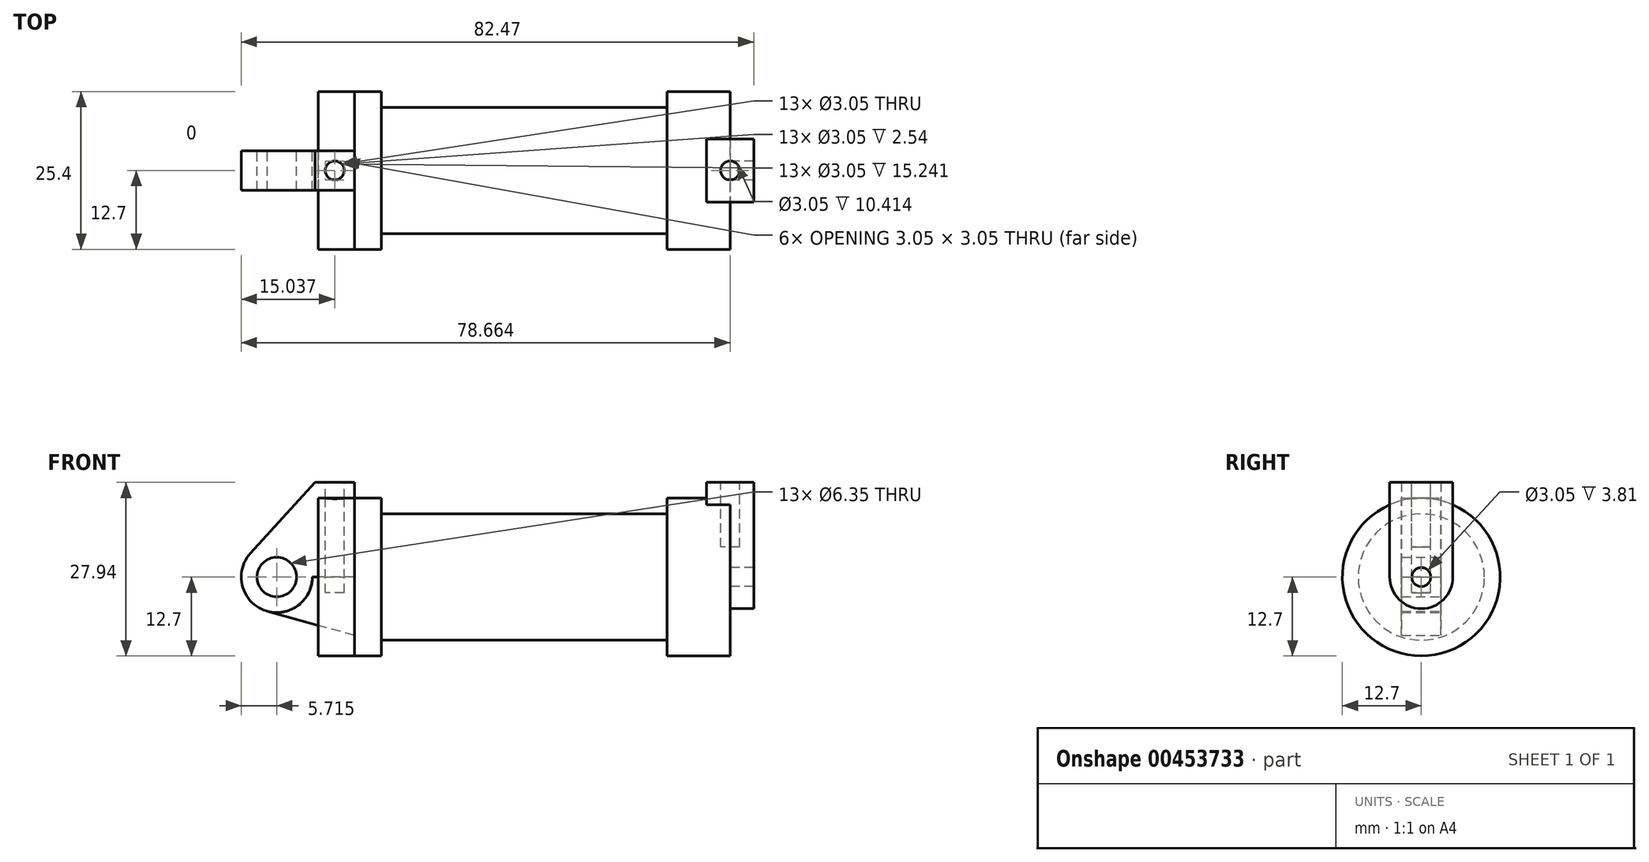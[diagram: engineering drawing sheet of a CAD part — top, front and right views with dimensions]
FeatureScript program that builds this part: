
annotation { "Feature Type Name" : "Feature", "Feature Type Description" : "" }
export const myFeature = defineFeature(function(context is Context, id is Id, definition is map)
    precondition{}
    {
        {
            var Q0;
            Q0=qCreatedBy(makeId("Front.planeOp"),FACE);
            var sketch = newSketch(context, id + "F0", { "sketchPlane" : qUnion([Q0])});
            skLineSegment(sketch, "E0", {"start": v(0, 0) * mm, "end": v(0, 12.7) * mm});
            skLineSegment(sketch, "E1", {"start": v(0, 12.7) * mm, "end": v(10.16, 12.7) * mm});
            skLineSegment(sketch, "E2", {"start": v(10.16, 12.7) * mm, "end": v(10.16, 10.16) * mm});
            skLineSegment(sketch, "E3", {"start": v(10.16, 10.16) * mm, "end": v(56.13, 10.16) * mm});
            skLineSegment(sketch, "E4", {"start": v(56.13, 10.16) * mm, "end": v(56.13, 12.7) * mm});
            skLineSegment(sketch, "E5", {"start": v(56.13, 12.7) * mm, "end": v(66.3, 12.7) * mm});
            skLineSegment(sketch, "E6", {"start": v(66.3, 12.7) * mm, "end": v(66.3, 0) * mm});
            skLineSegment(sketch, "E7", {"start": v(66.3, 0) * mm, "end": v(0, 0) * mm});
            skLineSegment(sketch, "E8", {"start": v(5.84, 15.24) * mm, "end": v(-0.5, 15.24) * mm});
            skLineSegment(sketch, "E9", {"start": v(-0.5, 15.24) * mm, "end": v(-10.88, 3.85) * mm});
            skLineSegment(sketch, "E10", {"start": v(0, 0) * mm, "end": v(-6.65, 0) * mm});
            skCircle(sketch, "E11", {"center": v(-6.65, 0) * mm, "radius": 5.72 * mm});
            skCircle(sketch, "E12", {"center": v(-6.65, 0) * mm, "radius": 3.18 * mm});
            skLineSegment(sketch, "E13", {"start": v(5.84, 15.24) * mm, "end": v(5.84, -9.4) * mm});
            skLineSegment(sketch, "E14", {"start": v(5.84, -9.4) * mm, "end": v(-8.18, -5.5) * mm});
            skSolve(sketch);
        }
        {
            var Q0;
            {var subQ1=sQuery(id+"F0.wireOp",EDGE,"E0");Q0=makeQuery(id+"F0.imprint","IMPRINT",FACE,{"disambiguationData":[TD([[makeQuery(id+"F0.imprint","IMPRINT",EDGE,{"derivedFrom":subQ1}),1.0]])]});}
            var Q1;
            Q1=makeQuery(id+"F0.imprint","IMPRINT",FACE,{"disambiguationData":[TD([[makeQuery(id+"F0.imprint","IMPRINT",EDGE,{"derivedFrom":sQuery(id+"F0.wireOp",EDGE,"E12")}),-1.0]])]});
            extrude(context, id + "F1", {"entities" : qUnion([Q0, Q1]), "endBound" : BoundingType.SYMMETRIC, "depth" : 6.35 * mm});
        }
        {
            var Q0;
            {var subQ0=sQuery(id+"F0.wireOp",EDGE,"E2");Q0=makeQuery(id+"F0.imprint","IMPRINT",FACE,{"disambiguationData":[TD([[makeQuery(id+"F0.imprint","IMPRINT",EDGE,{"derivedFrom":subQ0}),-1.0]])]});}
            var Q1;
            Q1=sQuery(id+"F0.wireOp",EDGE,"E10");
            revolve(context, id + "F2", {"entities" : qUnion([Q0]), "axis" : qUnion([Q1]), "revolveType" : RevolveType.TWO_DIRECTIONS, "angle" : 180 * degree, "angleBack" : 180 * degree});
        }
        {
            var Q0;
            {var subQ0=sQuery(id+"F0.wireOp",EDGE,"E0");Q0=makeQuery(id+"F0.imprint","IMPRINT",FACE,{"disambiguationData":[TD([[makeQuery(id+"F0.imprint","IMPRINT",EDGE,{"derivedFrom":subQ0}),-1.0]])]});}
            var Q1;
            Q1=sQuery(id+"F0.wireOp",EDGE,"E10");
            revolve(context, id + "F3", {"entities" : qUnion([Q0]), "axis" : qUnion([Q1]), "revolveType" : RevolveType.FULL});
        }
        {
            var Q0;
            {var subQ0=sQuery(id+"F0.wireOp",EDGE,"E14");Q0=makeQuery(id+"F0.imprint","IMPRINT",FACE,{"disambiguationData":[TD([[makeQuery(id+"F0.imprint","IMPRINT",EDGE,{"derivedFrom":subQ0}),-1.0]])]});}
            extrude(context, id + "F4", {"entities" : qUnion([Q0]), "endBound" : BoundingType.SYMMETRIC, "depth" : 6.35 * mm});
        }
        {
            var Q0;
            Q0=makeQuery(id+"F2.opRevolve","SWEPT_FACE",FACE,{"disambiguationData":[OSD([sQuery(id+"F0.wireOp",EDGE,"E6")])]});
            var sketch = newSketch(context, id + "F5", { "sketchPlane" : qUnion([Q0])});
            skCircle(sketch, "E15", {"center": v(0, 0) * mm, "radius": 5.08 * mm});
            skCircle(sketch, "E16", {"center": v(0, 0) * mm, "radius": 1.52 * mm});
            skLineSegment(sketch, "E17", {"start": v(5.08, 0) * mm, "end": v(5.08, 15.24) * mm});
            skLineSegment(sketch, "E18", {"start": v(-5.08, 0) * mm, "end": v(-5.08, 15.24) * mm});
            skLineSegment(sketch, "E19", {"start": v(-5.08, 15.24) * mm, "end": v(5.08, 15.24) * mm});
            skSolve(sketch);
        }
        {
            var Q0;
            Q0=qSketchRegion(id+"F5",true);
            extrude(context, id + "F6", {"entities" : qUnion([Q0]), "operationType" : NewBodyOperationType.ADD, "endBound" : BoundingType.SYMMETRIC, "depth" : 7.62 * mm});
        }
        {
            var Q0;
            Q0=makeQuery(id+"F6.opExtrude","SWEPT_FACE",FACE,{"disambiguationData":[OSD([sQuery(id+"F5.wireOp",EDGE,"E19")])]});
            var sketch = newSketch(context, id + "F7", { "sketchPlane" : qUnion([Q0])});
            skCircle(sketch, "E20", {"center": v(66.3, 0) * mm, "radius": 1.52 * mm});
            skPoint(sketch, "E20.centerSnap0", {"position": v(70.1, 0) * mm});
            skPoint(sketch, "E20.centerSnap1", {"position": v(66.3, 5.08) * mm});
            skSolve(sketch);
        }
        {
            var Q0;
            Q0=makeQuery(id+"F7.imprint","IMPRINT",FACE,{"disambiguationData":[TD([[makeQuery(id+"F7.imprint","IMPRINT",EDGE,{"derivedFrom":sQuery(id+"F7.wireOp",EDGE,"E20")}),1.0]])]});
            var Q1;
            Q1=sQuery(id+"F7.wireOp",EDGE,"E20");
            extrude(context, id + "F8", {"entities" : qUnion([Q0]), "operationType" : NewBodyOperationType.REMOVE, "surfaceEntities" : qUnion([Q1]), "oppositeDirection" : true, "depth" : 10.4 * mm});
        }
        {
            var Q0;
            Q0=makeQuery(id+"F1.opExtrude","SWEPT_FACE",FACE,{"disambiguationData":[OSD([sQuery(id+"F0.wireOp",EDGE,"E8")])]});
            var sketch = newSketch(context, id + "F9", { "sketchPlane" : qUnion([Q0])});
            skCircle(sketch, "E21", {"center": v(2.67, 0) * mm, "radius": 1.52 * mm});
            skPoint(sketch, "E21.centerSnap0", {"position": v(5.84, 0) * mm});
            skPoint(sketch, "E21.centerSnap1", {"position": v(2.67, 3.18) * mm});
            skSolve(sketch);
        }
        {
            var Q0;
            Q0=makeQuery(id+"F9.imprint","IMPRINT",FACE,{"disambiguationData":[TD([[makeQuery(id+"F9.imprint","IMPRINT",EDGE,{"derivedFrom":sQuery(id+"F9.wireOp",EDGE,"E21")}),1.0]])]});
            extrude(context, id + "F10", {"entities" : qUnion([Q0]), "operationType" : NewBodyOperationType.REMOVE, "oppositeDirection" : true, "depth" : 17.78 * mm});
        }
    });
